# Revit family: FU_Modular_Sandler_Chanel 5550
name_source: partatom
category: Furniture
units: mm (PartAtom-declared; Revit-internal decimal feet)

## family parameters
Always vertical = Yes
Cut with Voids When Loaded = No
OmniClass Number = 23.40.20.00
OmniClass Title = General Furniture and Specialties
Room Calculation Point = No
Shared = No
Work Plane-Based = No

## types (1)
- Chanel 5550
    Default Elevation = 0 mm  [stored 0 ft]
    Depth = 900 mm  [stored 2.95276 ft]
    Description = Square sofa module without backrest, solid wood frame, variable density foam. Webbed seat. Feet in black nylon.
    Height = 430 mm
    Manufacturer = Sandler
    Model = Chanel 5550
    URL = https://www.sandlerseating.com
    Upholstery = Fabric - Gravity - Frozen CPC27
    Width = 900 mm  [stored 2.95276 ft]

note: [stored X ft] marks values corroborated as IEEE doubles in the binary element streams (Revit-internal decimal feet)

## geometry (parser evidence)
native form markers: Sweep x3
no freeform markers — native parametric forms only
